# Revit family: Arper_Aava-02_trestle-fixed_wood_front-face-upholstery_7636
name_source: partatom
category: Furniture
units: mm (PartAtom-declared; Revit-internal decimal feet)

## family parameters
Always vertical = Yes
Cut with Voids When Loaded = No
OmniClass Number = 23.40.20.00
OmniClass Title = General Furniture and Specialties
Room Calculation Point = No
Shared = No
Work Plane-Based = No

## types (1)
- Arper_Aava-02_trestle-fixed_wood_front-face-upholstery_7636
    Default Elevation = 0 mm  [stored 0 ft]
    Description = Chair on fixed trestle base in powder-coated aluminium, mounted on 
self-braking castors (of the same colour as the base). Shell in 
plywood with a reconstituted oak or walnut finish, with front 
upholstery in fabric, leather, coated fabric or customer’s own
material. Optional armrests in the same colour as the base are also 
available, equipped with pads in wood in the same finish of the shell.
    Manufacturer = ARPER s.p.a.
    Model = Aava 02
    URL = http://www.arper.com

note: [stored X ft] marks values corroborated as IEEE doubles in the binary element streams (Revit-internal decimal feet)
